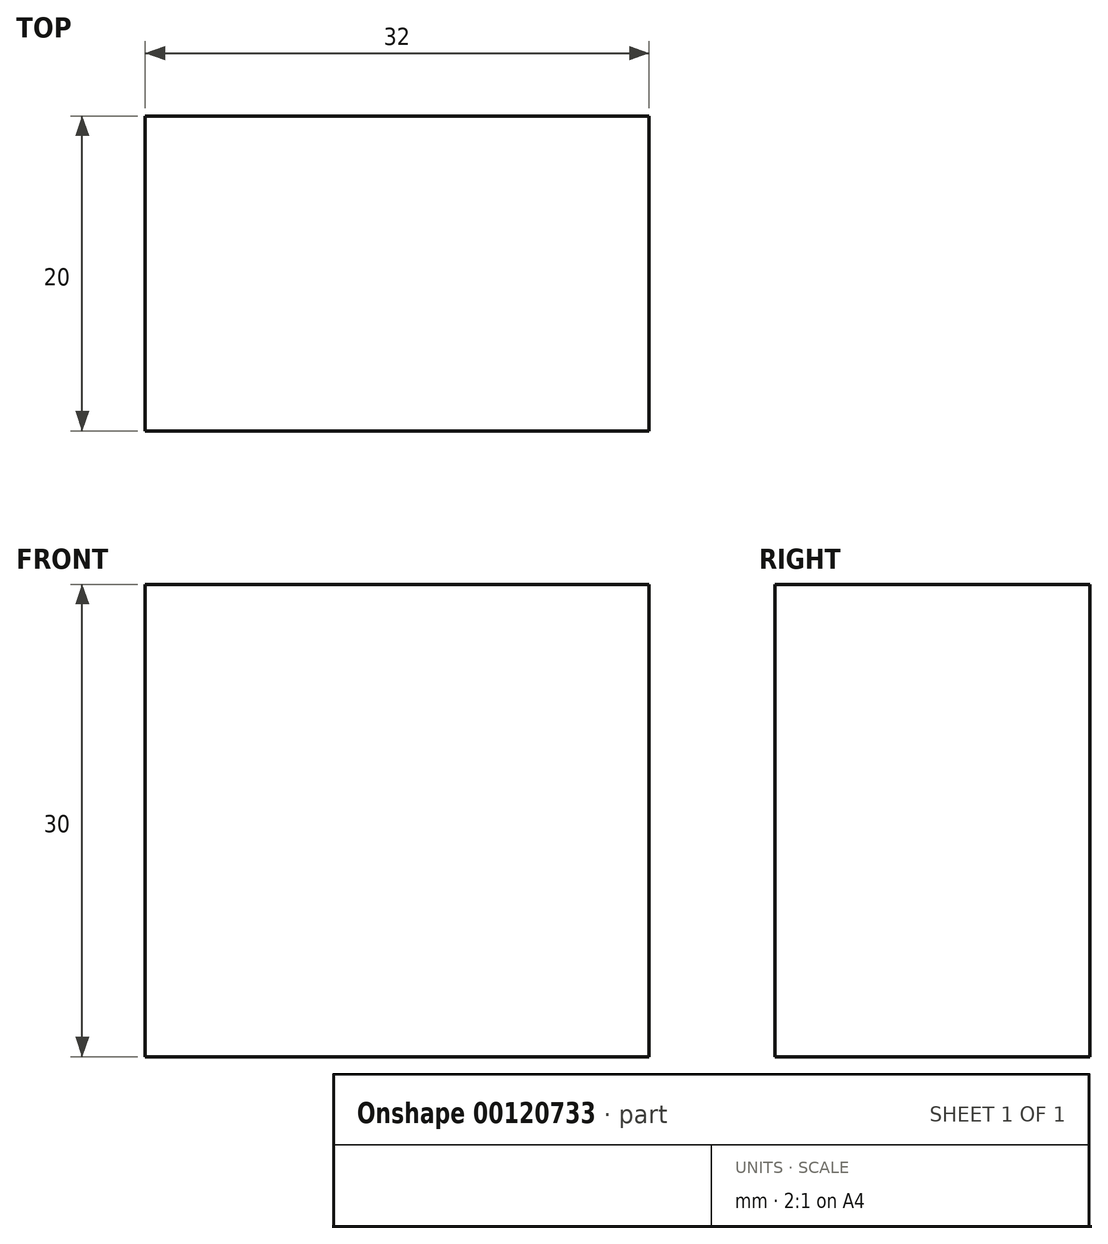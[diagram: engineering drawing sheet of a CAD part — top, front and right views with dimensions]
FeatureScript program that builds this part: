
annotation { "Feature Type Name" : "Feature", "Feature Type Description" : "" }
export const myFeature = defineFeature(function(context is Context, id is Id, definition is map)
    precondition{}
    {
        {
            var Q0;
            Q0=qCreatedBy(makeId("Front.planeOp"),FACE);
            var sketch = newSketch(context, id + "F0", { "sketchPlane" : qUnion([Q0])});
            skLineSegment(sketch, "E0.bottom", {"start": v(-1.68, 30.53) * mm, "end": v(30.32, 30.53) * mm});
            skLineSegment(sketch, "E0.top", {"start": v(-1.68, 0.53) * mm, "end": v(30.32, 0.53) * mm});
            skLineSegment(sketch, "E0.left", {"start": v(-1.68, 30.53) * mm, "end": v(-1.68, 0.53) * mm});
            skLineSegment(sketch, "E0.right", {"start": v(30.32, 30.53) * mm, "end": v(30.32, 0.53) * mm});
            skSolve(sketch);
        }
        {
            var Q0;
            Q0=qSketchRegion(id+"F0",true);
            extrude(context, id + "F1", {"entities" : qUnion([Q0]), "depth" : 20 * mm});
        }
    });
